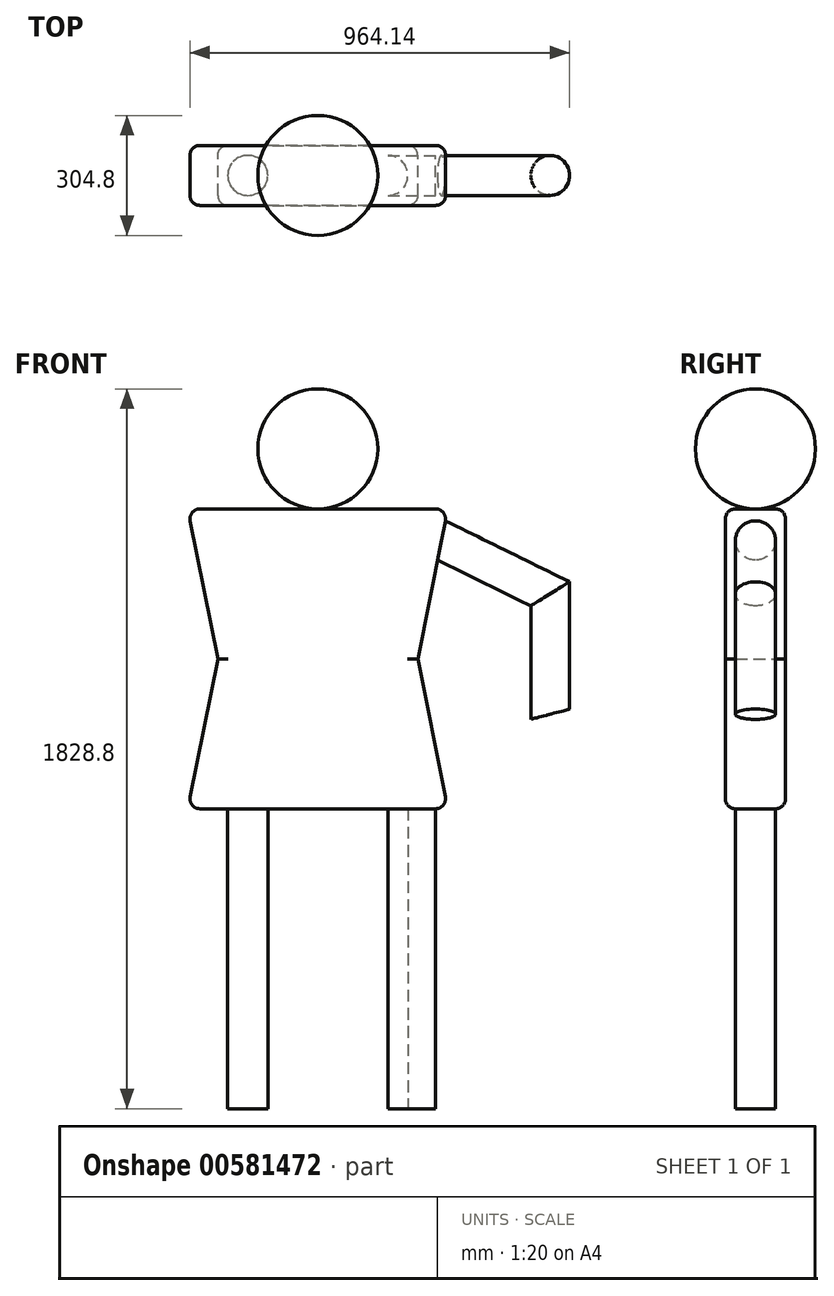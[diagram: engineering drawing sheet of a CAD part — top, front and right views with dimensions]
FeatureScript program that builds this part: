
annotation { "Feature Type Name" : "Feature", "Feature Type Description" : "" }
export const myFeature = defineFeature(function(context is Context, id is Id, definition is map)
    precondition{}
    {
        {
            var Q0;
            Q0=qCreatedBy(makeId("Front.planeOp"),FACE);
            var sketch = newSketch(context, id + "F0", { "sketchPlane" : qUnion([Q0])});
            skLineSegment(sketch, "E0", {"start": v(-330.2, 381) * mm, "end": v(-254, 0) * mm});
            skLineSegment(sketch, "E1", {"start": v(-254, 0) * mm, "end": v(-330.2, -381) * mm});
            skLineSegment(sketch, "E2", {"start": v(-330.2, -381) * mm, "end": v(330.2, -381) * mm});
            skLineSegment(sketch, "E3", {"start": v(330.2, -381) * mm, "end": v(254, 0) * mm});
            skLineSegment(sketch, "E4", {"start": v(254, 0) * mm, "end": v(330.2, 381) * mm});
            skLineSegment(sketch, "E5", {"start": v(330.2, 381) * mm, "end": v(-330.2, 381) * mm});
            skLineSegment(sketch, "E6", {"start": v(0, 381) * mm, "end": v(0, 685.8) * mm, "construction": true});
            skLineSegment(sketch, "E7", {"start": v(0, 685.8) * mm, "end": v(0, 381) * mm});
            skArc(sketch, "E8", {"start": v(0, 381) * mm, "mid": v(152.4, 533.4) * mm, "end": v(0, 685.8) * mm});
            skLineSegment(sketch, "E9", {"start": v(313.48, 297.41) * mm, "end": v(587.07, 163.06) * mm});
            skLineSegment(sketch, "E10", {"start": v(587.07, 163.06) * mm, "end": v(587.07, -141.74) * mm});
            skLineSegment(sketch, "E11", {"start": v(-228.6, -381) * mm, "end": v(-228.6, -1143) * mm});
            skLineSegment(sketch, "E12.MirrorCS", {"start": v(228.6, -381) * mm, "end": v(228.6, -1143) * mm});
            skSolve(sketch);
        }
        {
            var Q0;
            {var subQ0=sQuery(id+"F0.wireOp",EDGE,"E0");Q0=makeQuery(id+"F0.imprint","IMPRINT",FACE,{"disambiguationData":[TD([[makeQuery(id+"F0.imprint","IMPRINT",EDGE,{"derivedFrom":subQ0}),1.0]])]});}
            extrude(context, id + "F1", {"entities" : qUnion([Q0]), "endBound" : BoundingType.SYMMETRIC, "depth" : 152.4 * mm, "offsetDistance" : 25.4 * mm});
        }
        {
            var Q0;
            Q0=makeQuery(id+"F0.imprint","IMPRINT",FACE,{"disambiguationData":[TD([[makeQuery(id+"F0.imprint","IMPRINT",EDGE,{"derivedFrom":sQuery(id+"F0.wireOp",EDGE,"E7")}),1.0]])]});
            var Q1;
            Q1=sQuery(id+"F0.wireOp",EDGE,"E6");
            revolve(context, id + "F2", {"entities" : qUnion([Q0]), "axis" : qUnion([Q1]), "revolveType" : RevolveType.FULL});
        }
        {
            var Q0;
            Q0=makeQuery(id+"F1.opExtrude","CAP_EDGE",EDGE,{"disambiguationData":[OSD([sQuery(id+"F0.wireOp",EDGE,"E0")])],"isStart":false});
            var Q1;
            Q1=makeQuery(id+"F1.opExtrude","CAP_EDGE",EDGE,{"disambiguationData":[OSD([sQuery(id+"F0.wireOp",EDGE,"E5")])],"isStart":false});
            var Q2;
            Q2=makeQuery(id+"F1.opExtrude","SWEPT_EDGE",EDGE,{"disambiguationData":[OSD([sQuery(id+"F0.wireOp",EDGE,"E0"),sQuery(id+"F0.wireOp",EDGE,"E5")])]});
            var Q3;
            Q3=makeQuery(id+"F1.opExtrude","SWEPT_FACE",FACE,{"disambiguationData":[OSD([sQuery(id+"F0.wireOp",EDGE,"E5")])]});
            var Q4;
            Q4=makeQuery(id+"F1.opExtrude","CAP_EDGE",EDGE,{"disambiguationData":[OSD([sQuery(id+"F0.wireOp",EDGE,"E0")])],"isStart":true});
            var Q5;
            Q5=makeQuery(id+"F1.opExtrude","CAP_EDGE",EDGE,{"disambiguationData":[OSD([sQuery(id+"F0.wireOp",EDGE,"E1")])],"isStart":true});
            var Q6;
            Q6=makeQuery(id+"F1.opExtrude","CAP_EDGE",EDGE,{"disambiguationData":[OSD([sQuery(id+"F0.wireOp",EDGE,"E1")])],"isStart":false});
            var Q7;
            Q7=makeQuery(id+"F1.opExtrude","SWEPT_EDGE",EDGE,{"disambiguationData":[OSD([sQuery(id+"F0.wireOp",EDGE,"E1"),sQuery(id+"F0.wireOp",EDGE,"E2")])]});
            var Q8;
            Q8=makeQuery(id+"F1.opExtrude","CAP_EDGE",EDGE,{"disambiguationData":[OSD([sQuery(id+"F0.wireOp",EDGE,"E2")])],"isStart":false});
            var Q9;
            Q9=makeQuery(id+"F1.opExtrude","CAP_EDGE",EDGE,{"disambiguationData":[OSD([sQuery(id+"F0.wireOp",EDGE,"E4")])],"isStart":false});
            var Q10;
            Q10=makeQuery(id+"F1.opExtrude","CAP_EDGE",EDGE,{"disambiguationData":[OSD([sQuery(id+"F0.wireOp",EDGE,"E3")])],"isStart":false});
            var Q11;
            Q11=makeQuery(id+"F1.opExtrude","SWEPT_EDGE",EDGE,{"disambiguationData":[OSD([sQuery(id+"F0.wireOp",EDGE,"E2"),sQuery(id+"F0.wireOp",EDGE,"E3")])]});
            var Q12;
            Q12=makeQuery(id+"F1.opExtrude","CAP_EDGE",EDGE,{"disambiguationData":[OSD([sQuery(id+"F0.wireOp",EDGE,"E3")])],"isStart":true});
            var Q13;
            Q13=makeQuery(id+"F1.opExtrude","CAP_EDGE",EDGE,{"disambiguationData":[OSD([sQuery(id+"F0.wireOp",EDGE,"E4")])],"isStart":true});
            var Q14;
            Q14=makeQuery(id+"F1.opExtrude","CAP_EDGE",EDGE,{"disambiguationData":[OSD([sQuery(id+"F0.wireOp",EDGE,"E2")])],"isStart":true});
            var Q15;
            Q15=makeQuery(id+"F1.opExtrude","CAP_EDGE",EDGE,{"disambiguationData":[OSD([sQuery(id+"F0.wireOp",EDGE,"E5")])],"isStart":true});
            fillet(context, id + "F3", {"entities" : qUnion([Q0, Q1, Q2, Q3, Q4, Q5, Q6, Q7, Q8, Q9, Q10, Q11, Q12, Q13, Q14, Q15]), "radius" : 25.4 * mm, "tangentPropagation" : true, "allowEdgeOverflow" : false});
        }
        {
            var Q0;
            Q0=makeQuery(id+"F1.opExtrude","SWEPT_FACE",FACE,{"disambiguationData":[OSD([sQuery(id+"F0.wireOp",EDGE,"E4")])]});
            var sketch = newSketch(context, id + "F4", { "sketchPlane" : qUnion([Q0])});
            skCircle(sketch, "E13", {"center": v(0, 356.58) * mm, "radius": 50.8 * mm});
            skCircle(sketch, "E14.MirrorC", {"center": v(0, -2847.25) * mm, "radius": 50.8 * mm});
            skSolve(sketch);
        }
        {
            var Q0;
            {var subQ0=sQuery(id+"F4.wireOp",EDGE,"E13");var subQ1=sQuery(id+"F0.wireOp",EDGE,"E4");var subQ2=makeQuery(id+"F1.opExtrude","SWEPT_FACE",FACE,{"disambiguationData":[OSD([subQ1])]});var subQ4=makeQuery(id+"F4.imprint","INTERSECT",VERTEX,{"derivedFrom":[makeQuery(id+"F3.opFillet","BLEND_EDGE",EDGE,{"blendedFrom":[makeQuery(id+"F1.opExtrude","CAP_EDGE",EDGE,{"disambiguationData":[OSD([subQ1])],"isStart":true}),subQ2],"blendedInto":[subQ2]}),subQ0]});Q0=makeQuery(id+"F4.imprint","IMPRINT",FACE,{"disambiguationData":[TD([[makeQuery(id+"F4.imprint","IMPRINT",EDGE,{"disambiguationData":[TD([[subQ4,1.0]])],"derivedFrom":subQ0}),1.0]])]});}
            var Q1;
            Q1=sQuery(id+"F0.wireOp",EDGE,"E9");
            var Q2;
            Q2=sQuery(id+"F0.wireOp",EDGE,"E10");
            sweep(context, id + "F5", {"operationType" : NewBodyOperationType.ADD, "profiles" : qUnion([Q0]), "path" : qUnion([Q1, Q2])});
        }
        {
            var Q0;
            Q0=makeQuery(id+"F1.opExtrude","SWEPT_FACE",FACE,{"disambiguationData":[OSD([sQuery(id+"F0.wireOp",EDGE,"E2")])]});
            var sketch = newSketch(context, id + "F6", { "sketchPlane" : qUnion([Q0])});
            skCircle(sketch, "E15", {"center": v(-177.8, 0) * mm, "radius": 50.8 * mm});
            skCircle(sketch, "E16.MirrorC", {"center": v(177.8, 0) * mm, "radius": 50.8 * mm});
            skSolve(sketch);
        }
        {
            var Q0;
            {var subQ0=sQuery(id+"F6.wireOp",EDGE,"E15");var subQ1=sQuery(id+"F0.wireOp",EDGE,"E2");var subQ2=makeQuery(id+"F1.opExtrude","SWEPT_FACE",FACE,{"disambiguationData":[OSD([subQ1])]});var subQ4=makeQuery(id+"F6.imprint","INTERSECT",VERTEX,{"derivedFrom":[makeQuery(id+"F3.opFillet","BLEND_EDGE",EDGE,{"blendedFrom":[makeQuery(id+"F1.opExtrude","CAP_EDGE",EDGE,{"disambiguationData":[OSD([subQ1])],"isStart":false}),subQ2],"blendedInto":[subQ2]}),subQ0]});Q0=makeQuery(id+"F6.imprint","IMPRINT",FACE,{"disambiguationData":[TD([[makeQuery(id+"F6.imprint","IMPRINT",EDGE,{"disambiguationData":[TD([[subQ4,1.0]])],"derivedFrom":subQ0}),1.0]])]});}
            var Q1;
            {var subQ0=sQuery(id+"F6.wireOp",EDGE,"E16.MirrorC");var subQ1=sQuery(id+"F0.wireOp",EDGE,"E2");var subQ2=makeQuery(id+"F1.opExtrude","SWEPT_FACE",FACE,{"disambiguationData":[OSD([subQ1])]});var subQ4=makeQuery(id+"F6.imprint","INTERSECT",VERTEX,{"derivedFrom":[makeQuery(id+"F3.opFillet","BLEND_EDGE",EDGE,{"blendedFrom":[makeQuery(id+"F1.opExtrude","CAP_EDGE",EDGE,{"disambiguationData":[OSD([subQ1])],"isStart":false}),subQ2],"blendedInto":[subQ2]}),subQ0]});Q1=makeQuery(id+"F6.imprint","IMPRINT",FACE,{"disambiguationData":[TD([[makeQuery(id+"F6.imprint","IMPRINT",EDGE,{"disambiguationData":[TD([[subQ4,1.0]])],"derivedFrom":subQ0}),-1.0]])]});}
            var Q2;
            Q2=sQuery(id+"F0.wireOp",EDGE,"E11");
            sweep(context, id + "F7", {"operationType" : NewBodyOperationType.ADD, "profiles" : qUnion([Q0, Q1]), "path" : qUnion([Q2])});
        }
    });
